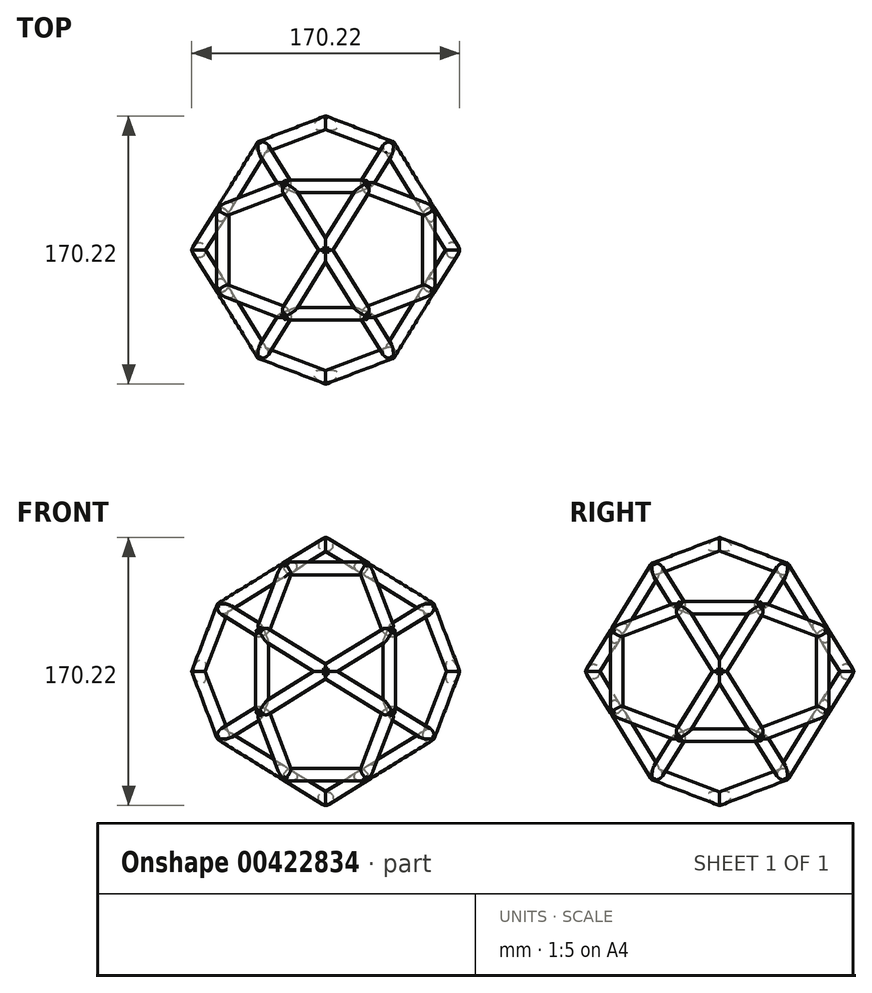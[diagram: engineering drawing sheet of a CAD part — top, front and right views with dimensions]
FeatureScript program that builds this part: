
annotation { "Feature Type Name" : "Feature", "Feature Type Description" : "" }
export const myFeature = defineFeature(function(context is Context, id is Id, definition is map)
    precondition{}
    {
        {
            var Q0;
            Q0=qCreatedBy(makeId("Top.planeOp"),FACE);
            var sketch = newSketch(context, id + "F0", { "sketchPlane" : qUnion([Q0])});
            skLineSegment(sketch, "E0", {"start": v(0, 80.9) * mm, "end": v(-40.45, 65.45) * mm});
            skLineSegment(sketch, "E1", {"start": v(-40.45, 65.45) * mm, "end": v(-80.9, 0) * mm});
            skLineSegment(sketch, "E2", {"start": v(-40.45, 65.45) * mm, "end": v(0, 65.45) * mm, "construction": true});
            skLineSegment(sketch, "E3.MirrorCS", {"start": v(0, -80.9) * mm, "end": v(-40.45, -65.45) * mm});
            skLineSegment(sketch, "E4.MirrorCS", {"start": v(-40.45, -65.45) * mm, "end": v(-80.9, 0) * mm});
            skLineSegment(sketch, "E5.MirrorCS", {"start": v(0, 80.9) * mm, "end": v(40.45, 65.45) * mm});
            skLineSegment(sketch, "E6.MirrorCS", {"start": v(40.45, 65.45) * mm, "end": v(80.9, 0) * mm});
            skLineSegment(sketch, "E7.MirrorCS", {"start": v(40.45, -65.45) * mm, "end": v(80.9, 0) * mm});
            skLineSegment(sketch, "E8.MirrorCS", {"start": v(0, -80.9) * mm, "end": v(40.45, -65.45) * mm});
            skLineSegment(sketch, "E9", {"start": v(0, 80.9) * mm, "end": v(0, 0) * mm, "construction": true});
            skLineSegment(sketch, "E10", {"start": v(0, 0) * mm, "end": v(-80.9, 0) * mm, "construction": true});
            skSolve(sketch);
        }
        {
            var Q0;
            Q0=qCreatedBy(makeId("Front.planeOp"),FACE);
            var sketch = newSketch(context, id + "F1", { "sketchPlane" : qUnion([Q0])});
            skLineSegment(sketch, "E11", {"start": v(0, 0) * mm, "end": v(0, 80.9) * mm, "construction": true});
            skSolve(sketch);
        }
        {
            var Q0;
            Q0=sQuery(id+"F1.wireOp",VERTEX,"E11.end");
            var Q1;
            Q1=sQuery(id+"F0.wireOp",VERTEX,"E2.start");
            var Q2;
            Q2=sQuery(id+"F0.wireOp",VERTEX,"E7.MirrorCS.start");
            cPlane(context, id + "F2", {"entities" : qUnion([Q0, Q1, Q2]), "cplaneType" : CPlaneType.THREE_POINT, "offset" : 25 * mm, "width" : 150 * mm, "height" : 150 * mm});
        }
        {
            var Q0;
            Q0=sQuery(id+"F1.wireOp",VERTEX,"E11.end");
            var Q1;
            Q1=sQuery(id+"F0.wireOp",VERTEX,"E4.MirrorCS.start");
            var Q2;
            Q2=sQuery(id+"F0.wireOp",VERTEX,"E6.MirrorCS.start");
            cPlane(context, id + "F3", {"entities" : qUnion([Q0, Q1, Q2]), "cplaneType" : CPlaneType.THREE_POINT, "offset" : 25 * mm, "width" : 150 * mm, "height" : 150 * mm});
        }
        {
            var Q0;
            Q0=qCreatedBy(id+"F2.planeOp",FACE);
            var sketch = newSketch(context, id + "F4", { "sketchPlane" : qUnion([Q0])});
            skLineSegment(sketch, "E12", {"start": v(0, 80.9) * mm, "end": v(-47.55, 65.45) * mm});
            skLineSegment(sketch, "E13", {"start": v(-47.55, 65.45) * mm, "end": v(-76.94, 25) * mm});
            skLineSegment(sketch, "E14", {"start": v(-76.94, 25) * mm, "end": v(-76.94, -25) * mm});
            skLineSegment(sketch, "E15.MirrorCS", {"start": v(0, -80.9) * mm, "end": v(-47.55, -65.45) * mm});
            skLineSegment(sketch, "E16.MirrorCS", {"start": v(-47.55, -65.45) * mm, "end": v(-76.94, -25) * mm});
            skLineSegment(sketch, "E17.MirrorCS", {"start": v(0, 80.9) * mm, "end": v(47.55, 65.45) * mm});
            skLineSegment(sketch, "E18.MirrorCS", {"start": v(47.55, 65.45) * mm, "end": v(76.94, 25) * mm});
            skLineSegment(sketch, "E19.MirrorCS", {"start": v(76.94, 25) * mm, "end": v(76.94, -25) * mm});
            skLineSegment(sketch, "E20.MirrorCS", {"start": v(47.55, -65.45) * mm, "end": v(76.94, -25) * mm});
            skLineSegment(sketch, "E21.MirrorCS", {"start": v(0, -80.9) * mm, "end": v(47.55, -65.45) * mm});
            skSolve(sketch);
        }
        {
            var Q0;
            Q0=qCreatedBy(id+"F3.planeOp",FACE);
            var sketch = newSketch(context, id + "F5", { "sketchPlane" : qUnion([Q0])});
            skLineSegment(sketch, "E22", {"start": v(0, 80.9) * mm, "end": v(47.55, 65.45) * mm});
            skLineSegment(sketch, "E23", {"start": v(47.55, 65.45) * mm, "end": v(76.94, 25) * mm});
            skLineSegment(sketch, "E24", {"start": v(76.94, 25) * mm, "end": v(76.94, -25) * mm});
            skLineSegment(sketch, "E25.MirrorCS", {"start": v(0, -80.9) * mm, "end": v(47.55, -65.45) * mm});
            skLineSegment(sketch, "E26.MirrorCS", {"start": v(47.55, -65.45) * mm, "end": v(76.94, -25) * mm});
            skLineSegment(sketch, "E27.MirrorCS", {"start": v(0, 80.9) * mm, "end": v(-47.55, 65.45) * mm});
            skLineSegment(sketch, "E28.MirrorCS", {"start": v(-47.55, 65.45) * mm, "end": v(-76.94, 25) * mm});
            skLineSegment(sketch, "E29.MirrorCS", {"start": v(-47.55, -65.45) * mm, "end": v(-76.94, -25) * mm});
            skLineSegment(sketch, "E30.MirrorCS", {"start": v(0, -80.9) * mm, "end": v(-47.55, -65.45) * mm});
            skLineSegment(sketch, "E31.MirrorCS", {"start": v(-76.94, 25) * mm, "end": v(-76.94, -25) * mm});
            skSolve(sketch);
        }
        {
            var Q0;
            Q0=sQuery(id+"F0.wireOp",VERTEX,"E8.MirrorCS.start");
            var Q1;
            Q1=sQuery(id+"F4.wireOp",VERTEX,"E16.MirrorCS.end");
            var Q2;
            Q2=sQuery(id+"F1.wireOp",VERTEX,"E11.start");
            cPlane(context, id + "F6", {"entities" : qUnion([Q0, Q1, Q2]), "cplaneType" : CPlaneType.THREE_POINT, "offset" : 25 * mm, "width" : 150 * mm, "height" : 150 * mm});
        }
        {
            var Q0;
            Q0=sQuery(id+"F0.wireOp",VERTEX,"E8.MirrorCS.start");
            var Q1;
            Q1=sQuery(id+"F5.wireOp",VERTEX,"E24.end");
            var Q2;
            Q2=sQuery(id+"F1.wireOp",VERTEX,"E11.start");
            cPlane(context, id + "F7", {"entities" : qUnion([Q0, Q1, Q2]), "cplaneType" : CPlaneType.THREE_POINT, "offset" : 25 * mm, "width" : 150 * mm, "height" : 150 * mm});
        }
        {
            var Q0;
            Q0=qCreatedBy(id+"F6.planeOp",FACE);
            var sketch = newSketch(context, id + "F8", { "sketchPlane" : qUnion([Q0])});
            skLineSegment(sketch, "E32", {"start": v(0, 80.9) * mm, "end": v(-47.55, 65.45) * mm});
            skLineSegment(sketch, "E33", {"start": v(-47.55, 65.45) * mm, "end": v(-76.94, 25) * mm});
            skLineSegment(sketch, "E34", {"start": v(-76.94, 25) * mm, "end": v(-76.94, -25) * mm});
            skLineSegment(sketch, "E35.MirrorCS", {"start": v(0, -80.9) * mm, "end": v(-47.55, -65.45) * mm});
            skLineSegment(sketch, "E36.MirrorCS", {"start": v(-47.55, -65.45) * mm, "end": v(-76.94, -25) * mm});
            skLineSegment(sketch, "E37.MirrorCS", {"start": v(0, 80.9) * mm, "end": v(47.55, 65.45) * mm});
            skLineSegment(sketch, "E38.MirrorCS", {"start": v(47.55, 65.45) * mm, "end": v(76.94, 25) * mm});
            skLineSegment(sketch, "E39.MirrorCS", {"start": v(76.94, 25) * mm, "end": v(76.94, -25) * mm});
            skLineSegment(sketch, "E40.MirrorCS", {"start": v(47.55, -65.45) * mm, "end": v(76.94, -25) * mm});
            skLineSegment(sketch, "E41.MirrorCS", {"start": v(0, -80.9) * mm, "end": v(47.55, -65.45) * mm});
            skSolve(sketch);
        }
        {
            var Q0;
            Q0=qCreatedBy(id+"F7.planeOp",FACE);
            var sketch = newSketch(context, id + "F9", { "sketchPlane" : qUnion([Q0])});
            skLineSegment(sketch, "E42", {"start": v(0, -80.9) * mm, "end": v(-47.55, -65.45) * mm});
            skLineSegment(sketch, "E43", {"start": v(-47.55, -65.45) * mm, "end": v(-76.94, -25) * mm});
            skLineSegment(sketch, "E44", {"start": v(-76.94, -25) * mm, "end": v(-76.94, 25) * mm});
            skLineSegment(sketch, "E45.MirrorCS", {"start": v(0, 80.9) * mm, "end": v(-47.55, 65.45) * mm});
            skLineSegment(sketch, "E46.MirrorCS", {"start": v(-47.55, 65.45) * mm, "end": v(-76.94, 25) * mm});
            skLineSegment(sketch, "E47.MirrorCS", {"start": v(0, -80.9) * mm, "end": v(47.55, -65.45) * mm});
            skLineSegment(sketch, "E48.MirrorCS", {"start": v(47.55, -65.45) * mm, "end": v(76.94, -25) * mm});
            skLineSegment(sketch, "E49.MirrorCS", {"start": v(76.94, -25) * mm, "end": v(76.94, 25) * mm});
            skLineSegment(sketch, "E50.MirrorCS", {"start": v(47.55, 65.45) * mm, "end": v(76.94, 25) * mm});
            skLineSegment(sketch, "E51.MirrorCS", {"start": v(0, 80.9) * mm, "end": v(47.55, 65.45) * mm});
            skSolve(sketch);
        }
        {
            var Q0;
            Q0=sQuery(id+"F0.wireOp",VERTEX,"E7.MirrorCS.end");
            var Q1;
            Q1=sQuery(id+"F9.wireOp",VERTEX,"E46.MirrorCS.end");
            var Q2;
            Q2=sQuery(id+"F1.wireOp",VERTEX,"E11.start");
            cPlane(context, id + "F10", {"entities" : qUnion([Q0, Q1, Q2]), "cplaneType" : CPlaneType.THREE_POINT, "offset" : 25 * mm, "width" : 150 * mm, "height" : 150 * mm});
        }
        {
            var Q0;
            Q0=sQuery(id+"F0.wireOp",VERTEX,"E7.MirrorCS.end");
            var Q1;
            Q1=sQuery(id+"F1.wireOp",VERTEX,"E11.start");
            var Q2;
            Q2=sQuery(id+"F8.wireOp",VERTEX,"E34.end");
            cPlane(context, id + "F11", {"entities" : qUnion([Q0, Q1, Q2]), "cplaneType" : CPlaneType.THREE_POINT, "offset" : 25 * mm, "width" : 150 * mm, "height" : 150 * mm});
        }
        {
            var Q0;
            Q0=qCreatedBy(id+"F10.planeOp",FACE);
            var sketch = newSketch(context, id + "F12", { "sketchPlane" : qUnion([Q0])});
            skLineSegment(sketch, "E52", {"start": v(80.9, 0) * mm, "end": v(65.45, -47.55) * mm});
            skLineSegment(sketch, "E53", {"start": v(65.45, -47.55) * mm, "end": v(25, -76.94) * mm});
            skLineSegment(sketch, "E54", {"start": v(25, -76.94) * mm, "end": v(-25, -76.94) * mm});
            skLineSegment(sketch, "E55.MirrorCS", {"start": v(-80.9, 0) * mm, "end": v(-65.45, -47.55) * mm});
            skLineSegment(sketch, "E56.MirrorCS", {"start": v(-65.45, -47.55) * mm, "end": v(-25, -76.94) * mm});
            skLineSegment(sketch, "E57.MirrorCS", {"start": v(80.9, 0) * mm, "end": v(65.45, 47.55) * mm});
            skLineSegment(sketch, "E58.MirrorCS", {"start": v(65.45, 47.55) * mm, "end": v(25, 76.94) * mm});
            skLineSegment(sketch, "E59.MirrorCS", {"start": v(25, 76.94) * mm, "end": v(-25, 76.94) * mm});
            skLineSegment(sketch, "E60.MirrorCS", {"start": v(-65.45, 47.55) * mm, "end": v(-25, 76.94) * mm});
            skLineSegment(sketch, "E61.MirrorCS", {"start": v(-80.9, 0) * mm, "end": v(-65.45, 47.55) * mm});
            skSolve(sketch);
        }
        {
            var Q0;
            Q0=qCreatedBy(id+"F11.planeOp",FACE);
            var sketch = newSketch(context, id + "F13", { "sketchPlane" : qUnion([Q0])});
            skLineSegment(sketch, "E62", {"start": v(80.9, 0) * mm, "end": v(65.45, -47.55) * mm});
            skLineSegment(sketch, "E63", {"start": v(65.45, -47.55) * mm, "end": v(25, -76.94) * mm});
            skLineSegment(sketch, "E64", {"start": v(25, -76.94) * mm, "end": v(-25, -76.94) * mm});
            skLineSegment(sketch, "E65.MirrorCS", {"start": v(-80.9, 0) * mm, "end": v(-65.45, -47.55) * mm});
            skLineSegment(sketch, "E66.MirrorCS", {"start": v(-65.45, -47.55) * mm, "end": v(-25, -76.94) * mm});
            skLineSegment(sketch, "E67.MirrorCS", {"start": v(80.9, 0) * mm, "end": v(65.45, 47.55) * mm});
            skLineSegment(sketch, "E68.MirrorCS", {"start": v(65.45, 47.55) * mm, "end": v(25, 76.94) * mm});
            skLineSegment(sketch, "E69.MirrorCS", {"start": v(25, 76.94) * mm, "end": v(-25, 76.94) * mm});
            skLineSegment(sketch, "E70.MirrorCS", {"start": v(-65.45, 47.55) * mm, "end": v(-25, 76.94) * mm});
            skLineSegment(sketch, "E71.MirrorCS", {"start": v(-80.9, 0) * mm, "end": v(-65.45, 47.55) * mm});
            skSolve(sketch);
        }
        {
            var Q0;
            Q0=sQuery(id+"F4.wireOp",EDGE,"E12");
            cPlane(context, id + "F14", {"entities" : qUnion([Q0]), "cplaneType" : CPlaneType.MID_PLANE, "offset" : 25 * mm, "width" : 150 * mm, "height" : 150 * mm});
        }
        {
            var Q0;
            Q0=qCreatedBy(id+"F14.planeOp",FACE);
            var sketch = newSketch(context, id + "F15", { "sketchPlane" : qUnion([Q0])});
            skCircle(sketch, "E72", {"center": v(14.43, 75.58) * mm, "radius": 4 * mm});
            skSolve(sketch);
        }
        {
            var Q0;
            Q0=sQuery(id+"F5.wireOp",EDGE,"E22");
            cPlane(context, id + "F16", {"entities" : qUnion([Q0]), "cplaneType" : CPlaneType.MID_PLANE, "offset" : 25 * mm, "width" : 150 * mm, "height" : 150 * mm});
        }
        {
            var Q0;
            Q0=qCreatedBy(id+"F16.planeOp",FACE);
            var sketch = newSketch(context, id + "F17", { "sketchPlane" : qUnion([Q0])});
            skCircle(sketch, "E73", {"center": v(-14.43, 75.58) * mm, "radius": 4 * mm});
            skSolve(sketch);
        }
        {
            var Q0;
            Q0=sQuery(id+"F12.wireOp",EDGE,"E59.MirrorCS");
            cPlane(context, id + "F18", {"entities" : qUnion([Q0]), "cplaneType" : CPlaneType.MID_PLANE, "offset" : 25 * mm, "width" : 150 * mm, "height" : 150 * mm});
        }
        {
            var Q0;
            Q0=qCreatedBy(id+"F18.planeOp",FACE);
            var sketch = newSketch(context, id + "F19", { "sketchPlane" : qUnion([Q0])});
            skCircle(sketch, "E74", {"center": v(40.45, 65.45) * mm, "radius": 4 * mm});
            skSolve(sketch);
        }
        {
            var Q0;
            Q0=sQuery(id+"F8.wireOp",EDGE,"E32");
            cPlane(context, id + "F20", {"entities" : qUnion([Q0]), "cplaneType" : CPlaneType.MID_PLANE, "offset" : 25 * mm, "width" : 150 * mm, "height" : 150 * mm});
        }
        {
            var Q0;
            Q0=qCreatedBy(id+"F20.planeOp",FACE);
            var sketch = newSketch(context, id + "F21", { "sketchPlane" : qUnion([Q0])});
            skCircle(sketch, "E75", {"center": v(76.94, 0) * mm, "radius": 4 * mm});
            skSolve(sketch);
        }
        {
            var Q0;
            Q0=sQuery(id+"F9.wireOp",EDGE,"E42");
            cPlane(context, id + "F22", {"entities" : qUnion([Q0]), "cplaneType" : CPlaneType.MID_PLANE, "offset" : 25 * mm, "width" : 150 * mm, "height" : 150 * mm});
        }
        {
            var Q0;
            Q0=qCreatedBy(id+"F22.planeOp",FACE);
            var sketch = newSketch(context, id + "F23", { "sketchPlane" : qUnion([Q0])});
            skCircle(sketch, "E76", {"center": v(76.94, 0) * mm, "radius": 4 * mm});
            skSolve(sketch);
        }
        {
            var Q0;
            Q0=makeQuery(id+"F17.imprint","IMPRINT",FACE,{"disambiguationData":[TD([[makeQuery(id+"F17.imprint","IMPRINT",EDGE,{"derivedFrom":sQuery(id+"F17.wireOp",EDGE,"E73")}),1.0]])]});
            var Q1;
            Q1=sQuery(id+"F5.wireOp",EDGE,"E22");
            var Q2;
            Q2=sQuery(id+"F5.wireOp",EDGE,"E23");
            var Q3;
            Q3=sQuery(id+"F5.wireOp",EDGE,"E24");
            var Q4;
            Q4=sQuery(id+"F5.wireOp",EDGE,"E26.MirrorCS");
            var Q5;
            Q5=sQuery(id+"F5.wireOp",EDGE,"E25.MirrorCS");
            var Q6;
            Q6=sQuery(id+"F5.wireOp",EDGE,"E30.MirrorCS");
            var Q7;
            Q7=sQuery(id+"F5.wireOp",EDGE,"E29.MirrorCS");
            var Q8;
            Q8=sQuery(id+"F5.wireOp",EDGE,"E31.MirrorCS");
            var Q9;
            Q9=sQuery(id+"F5.wireOp",EDGE,"E28.MirrorCS");
            var Q10;
            Q10=sQuery(id+"F5.wireOp",EDGE,"E27.MirrorCS");
            sweep(context, id + "F24", {"profiles" : qUnion([Q0]), "path" : qUnion([Q1, Q2, Q3, Q4, Q5, Q6, Q7, Q8, Q9, Q10])});
        }
        {
            var Q0;
            Q0=makeQuery(id+"F15.imprint","IMPRINT",FACE,{"disambiguationData":[TD([[makeQuery(id+"F15.imprint","IMPRINT",EDGE,{"derivedFrom":sQuery(id+"F15.wireOp",EDGE,"E72")}),1.0]])]});
            var Q1;
            Q1=sQuery(id+"F15.wireOp",EDGE,"E72");
            var Q2;
            Q2=sQuery(id+"F4.wireOp",EDGE,"E12");
            var Q3;
            Q3=sQuery(id+"F4.wireOp",EDGE,"E13");
            var Q4;
            Q4=sQuery(id+"F4.wireOp",EDGE,"E14");
            var Q5;
            Q5=sQuery(id+"F4.wireOp",EDGE,"E16.MirrorCS");
            var Q6;
            Q6=sQuery(id+"F4.wireOp",EDGE,"E15.MirrorCS");
            var Q7;
            Q7=sQuery(id+"F4.wireOp",EDGE,"E21.MirrorCS");
            var Q8;
            Q8=sQuery(id+"F4.wireOp",EDGE,"E20.MirrorCS");
            var Q9;
            Q9=sQuery(id+"F4.wireOp",EDGE,"E19.MirrorCS");
            var Q10;
            Q10=sQuery(id+"F4.wireOp",EDGE,"E18.MirrorCS");
            var Q11;
            Q11=sQuery(id+"F4.wireOp",EDGE,"E17.MirrorCS");
            sweep(context, id + "F25", {"operationType" : NewBodyOperationType.ADD, "profiles" : qUnion([Q0]), "surfaceProfiles" : qUnion([Q1]), "path" : qUnion([Q2, Q3, Q4, Q5, Q6, Q7, Q8, Q9, Q10, Q11])});
        }
        {
            var Q0;
            Q0=makeQuery(id+"F19.imprint","IMPRINT",FACE,{"disambiguationData":[TD([[makeQuery(id+"F19.imprint","IMPRINT",EDGE,{"derivedFrom":sQuery(id+"F19.wireOp",EDGE,"E74")}),1.0]])]});
            var Q1;
            Q1=sQuery(id+"F19.wireOp",EDGE,"E74");
            var Q2;
            Q2=sQuery(id+"F12.wireOp",EDGE,"E59.MirrorCS");
            var Q3;
            Q3=sQuery(id+"F12.wireOp",EDGE,"E60.MirrorCS");
            var Q4;
            Q4=sQuery(id+"F12.wireOp",EDGE,"E61.MirrorCS");
            var Q5;
            Q5=sQuery(id+"F12.wireOp",EDGE,"E55.MirrorCS");
            var Q6;
            Q6=sQuery(id+"F12.wireOp",EDGE,"E56.MirrorCS");
            var Q7;
            Q7=sQuery(id+"F12.wireOp",EDGE,"E54");
            var Q8;
            Q8=sQuery(id+"F12.wireOp",EDGE,"E53");
            var Q9;
            Q9=sQuery(id+"F12.wireOp",EDGE,"E52");
            var Q10;
            Q10=sQuery(id+"F12.wireOp",EDGE,"E57.MirrorCS");
            var Q11;
            Q11=sQuery(id+"F12.wireOp",EDGE,"E58.MirrorCS");
            sweep(context, id + "F26", {"operationType" : NewBodyOperationType.ADD, "profiles" : qUnion([Q0]), "surfaceProfiles" : qUnion([Q1]), "path" : qUnion([Q2, Q3, Q4, Q5, Q6, Q7, Q8, Q9, Q10, Q11])});
        }
        {
            var Q0;
            Q0=makeQuery(id+"F23.imprint","IMPRINT",FACE,{"disambiguationData":[TD([[makeQuery(id+"F23.imprint","IMPRINT",EDGE,{"derivedFrom":sQuery(id+"F23.wireOp",EDGE,"E76")}),1.0]])]});
            var Q1;
            Q1=sQuery(id+"F23.wireOp",EDGE,"E76");
            var Q2;
            Q2=sQuery(id+"F9.wireOp",EDGE,"E42");
            var Q3;
            Q3=sQuery(id+"F9.wireOp",EDGE,"E43");
            var Q4;
            Q4=sQuery(id+"F9.wireOp",EDGE,"E44");
            var Q5;
            Q5=sQuery(id+"F9.wireOp",EDGE,"E46.MirrorCS");
            var Q6;
            Q6=sQuery(id+"F9.wireOp",EDGE,"E45.MirrorCS");
            var Q7;
            Q7=sQuery(id+"F9.wireOp",EDGE,"E51.MirrorCS");
            var Q8;
            Q8=sQuery(id+"F9.wireOp",EDGE,"E50.MirrorCS");
            var Q9;
            Q9=sQuery(id+"F9.wireOp",EDGE,"E49.MirrorCS");
            var Q10;
            Q10=sQuery(id+"F9.wireOp",EDGE,"E48.MirrorCS");
            var Q11;
            Q11=sQuery(id+"F9.wireOp",EDGE,"E47.MirrorCS");
            sweep(context, id + "F27", {"operationType" : NewBodyOperationType.ADD, "profiles" : qUnion([Q0]), "surfaceProfiles" : qUnion([Q1]), "path" : qUnion([Q2, Q3, Q4, Q5, Q6, Q7, Q8, Q9, Q10, Q11])});
        }
        {
            var Q0;
            Q0=makeQuery(id+"F21.imprint","IMPRINT",FACE,{"disambiguationData":[TD([[makeQuery(id+"F21.imprint","IMPRINT",EDGE,{"derivedFrom":sQuery(id+"F21.wireOp",EDGE,"E75")}),1.0]])]});
            var Q1;
            Q1=sQuery(id+"F21.wireOp",EDGE,"E75");
            var Q2;
            Q2=sQuery(id+"F8.wireOp",EDGE,"E32");
            var Q3;
            Q3=sQuery(id+"F8.wireOp",EDGE,"E33");
            var Q4;
            Q4=sQuery(id+"F8.wireOp",EDGE,"E34");
            var Q5;
            Q5=sQuery(id+"F8.wireOp",EDGE,"E36.MirrorCS");
            var Q6;
            Q6=sQuery(id+"F8.wireOp",EDGE,"E35.MirrorCS");
            var Q7;
            Q7=sQuery(id+"F8.wireOp",EDGE,"E41.MirrorCS");
            var Q8;
            Q8=sQuery(id+"F8.wireOp",EDGE,"E40.MirrorCS");
            var Q9;
            Q9=sQuery(id+"F8.wireOp",EDGE,"E39.MirrorCS");
            var Q10;
            Q10=sQuery(id+"F8.wireOp",EDGE,"E38.MirrorCS");
            var Q11;
            Q11=sQuery(id+"F8.wireOp",EDGE,"E37.MirrorCS");
            sweep(context, id + "F28", {"operationType" : NewBodyOperationType.ADD, "profiles" : qUnion([Q0]), "surfaceProfiles" : qUnion([Q1]), "path" : qUnion([Q2, Q3, Q4, Q5, Q6, Q7, Q8, Q9, Q10, Q11])});
        }
        {
            var Q0;
            Q0=sQuery(id+"F13.wireOp",EDGE,"E69.MirrorCS");
            cPlane(context, id + "F29", {"entities" : qUnion([Q0]), "cplaneType" : CPlaneType.MID_PLANE, "offset" : 25 * mm, "width" : 150 * mm, "height" : 150 * mm});
        }
        {
            var Q0;
            Q0=qCreatedBy(id+"F29.planeOp",FACE);
            var sketch = newSketch(context, id + "F30", { "sketchPlane" : qUnion([Q0])});
            skCircle(sketch, "E77", {"center": v(-40.45, 65.45) * mm, "radius": 4 * mm});
            skSolve(sketch);
        }
        {
            var Q0;
            Q0=makeQuery(id+"F30.imprint","IMPRINT",FACE,{"disambiguationData":[TD([[makeQuery(id+"F30.imprint","IMPRINT",EDGE,{"derivedFrom":sQuery(id+"F30.wireOp",EDGE,"E77")}),1.0]])]});
            var Q1;
            Q1=sQuery(id+"F13.wireOp",EDGE,"E69.MirrorCS");
            var Q2;
            Q2=sQuery(id+"F13.wireOp",EDGE,"E68.MirrorCS");
            var Q3;
            Q3=sQuery(id+"F13.wireOp",EDGE,"E67.MirrorCS");
            var Q4;
            Q4=sQuery(id+"F13.wireOp",EDGE,"E62");
            var Q5;
            Q5=sQuery(id+"F13.wireOp",EDGE,"E63");
            var Q6;
            Q6=sQuery(id+"F13.wireOp",EDGE,"E64");
            var Q7;
            Q7=sQuery(id+"F13.wireOp",EDGE,"E66.MirrorCS");
            var Q8;
            Q8=sQuery(id+"F13.wireOp",EDGE,"E65.MirrorCS");
            var Q9;
            Q9=sQuery(id+"F13.wireOp",EDGE,"E71.MirrorCS");
            var Q10;
            Q10=sQuery(id+"F13.wireOp",EDGE,"E70.MirrorCS");
            sweep(context, id + "F31", {"operationType" : NewBodyOperationType.ADD, "profiles" : qUnion([Q0]), "path" : qUnion([Q1, Q2, Q3, Q4, Q5, Q6, Q7, Q8, Q9, Q10])});
        }
    });
